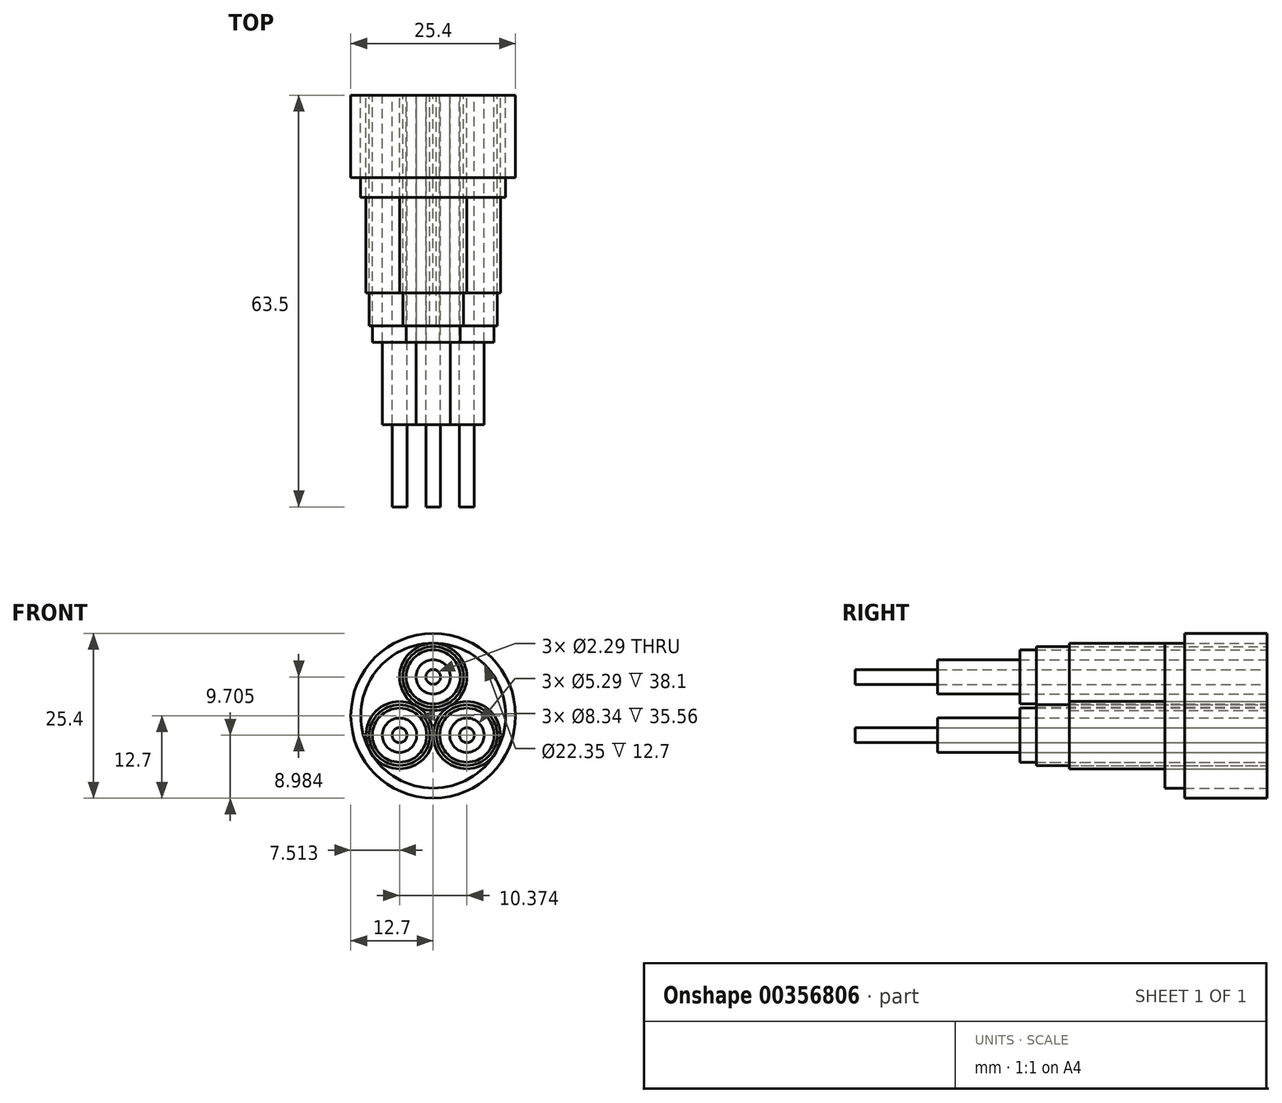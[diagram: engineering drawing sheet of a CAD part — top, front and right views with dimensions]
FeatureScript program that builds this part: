
annotation { "Feature Type Name" : "Feature", "Feature Type Description" : "" }
export const myFeature = defineFeature(function(context is Context, id is Id, definition is map)
    precondition{}
    {
        {
            var Q0;
            Q0=qCreatedBy(makeId("Front.planeOp"),FACE);
            var sketch = newSketch(context, id + "F0", { "sketchPlane" : qUnion([Q0])});
            skCircle(sketch, "E0", {"center": v(0, 0) * mm, "radius": 12.7 * mm});
            skCircle(sketch, "E1", {"center": v(0, 0) * mm, "radius": 11.18 * mm});
            skCircle(sketch, "E2", {"center": v(0, 5.99) * mm, "radius": 5.19 * mm});
            skCircle(sketch, "E3.1.0", {"center": v(-5.19, -3) * mm, "radius": 5.19 * mm, "construction": true});
            skCircle(sketch, "E3.2.0", {"center": v(5.19, -3) * mm, "radius": 5.19 * mm, "construction": true});
            skCircle(sketch, "E4", {"center": v(0, 5.99) * mm, "radius": 4.68 * mm});
            skCircle(sketch, "E5", {"center": v(0, 5.99) * mm, "radius": 4.17 * mm});
            skCircle(sketch, "E6", {"center": v(0, 5.99) * mm, "radius": 2.65 * mm});
            skCircle(sketch, "E7", {"center": v(0, 5.99) * mm, "radius": 1.14 * mm});
            skSolve(sketch);
        }
        {
            var Q0;
            Q0 = qSketchRegion(id + "F0", true);
            extrude(context, id + "F1", {"entities" : qUnion([Q0]), "depth" : 12.7 * mm});
        }
        {
            var Q0;
            Q0=makeQuery(id+"F0.imprint","IMPRINT",FACE,{"disambiguationData":[TD([[makeQuery(id+"F0.imprint","IMPRINT",EDGE,{"derivedFrom":sQuery(id+"F0.wireOp",EDGE,"E1")}),1.0]])]});
            var Q1;
            Q1=makeQuery(id+"F0.imprint","IMPRINT",FACE,{"disambiguationData":[TD([[makeQuery(id+"F0.imprint","IMPRINT",EDGE,{"derivedFrom":sQuery(id+"F0.wireOp",EDGE,"E7")}),1.0]])]});
            var Q2;
            Q2=makeQuery(id+"F0.imprint","IMPRINT",FACE,{"disambiguationData":[TD([[makeQuery(id+"F0.imprint","IMPRINT",EDGE,{"derivedFrom":sQuery(id+"F0.wireOp",EDGE,"E4")}),1.0]])]});
            var Q3;
            Q3=makeQuery(id+"F0.imprint","IMPRINT",FACE,{"disambiguationData":[TD([[makeQuery(id+"F0.imprint","IMPRINT",EDGE,{"derivedFrom":sQuery(id+"F0.wireOp",EDGE,"E5")}),1.0]])]});
            var Q4;
            Q4=makeQuery(id+"F0.imprint","IMPRINT",FACE,{"disambiguationData":[TD([[makeQuery(id+"F0.imprint","IMPRINT",EDGE,{"derivedFrom":sQuery(id+"F0.wireOp",EDGE,"E6")}),1.0]])]});
            var Q5;
            Q5=makeQuery(id+"F0.imprint","IMPRINT",FACE,{"disambiguationData":[TD([[makeQuery(id+"F0.imprint","IMPRINT",EDGE,{"derivedFrom":sQuery(id+"F0.wireOp",EDGE,"E2")}),1.0]])]});
            extrude(context, id + "F2", {"entities" : qUnion([Q0, Q1, Q2, Q3, Q4, Q5]), "depth" : 15.75 * mm});
        }
        {
            var Q0;
            Q0=makeQuery(id+"F0.imprint","IMPRINT",FACE,{"disambiguationData":[TD([[makeQuery(id+"F0.imprint","IMPRINT",EDGE,{"derivedFrom":sQuery(id+"F0.wireOp",EDGE,"E7")}),1.0]])]});
            var Q1;
            Q1=makeQuery(id+"F0.imprint","IMPRINT",FACE,{"disambiguationData":[TD([[makeQuery(id+"F0.imprint","IMPRINT",EDGE,{"derivedFrom":sQuery(id+"F0.wireOp",EDGE,"E2")}),1.0]])]});
            var Q2;
            Q2=makeQuery(id+"F0.imprint","IMPRINT",FACE,{"disambiguationData":[TD([[makeQuery(id+"F0.imprint","IMPRINT",EDGE,{"derivedFrom":sQuery(id+"F0.wireOp",EDGE,"E4")}),1.0]])]});
            var Q3;
            Q3=makeQuery(id+"F0.imprint","IMPRINT",FACE,{"disambiguationData":[TD([[makeQuery(id+"F0.imprint","IMPRINT",EDGE,{"derivedFrom":sQuery(id+"F0.wireOp",EDGE,"E5")}),1.0]])]});
            var Q4;
            Q4=makeQuery(id+"F0.imprint","IMPRINT",FACE,{"disambiguationData":[TD([[makeQuery(id+"F0.imprint","IMPRINT",EDGE,{"derivedFrom":sQuery(id+"F0.wireOp",EDGE,"E6")}),1.0]])]});
            extrude(context, id + "F3", {"entities" : qUnion([Q0, Q1, Q2, Q3, Q4]), "depth" : 30.48 * mm});
        }
        {
            var Q0;
            Q0=makeQuery(id+"F0.imprint","IMPRINT",FACE,{"disambiguationData":[TD([[makeQuery(id+"F0.imprint","IMPRINT",EDGE,{"derivedFrom":sQuery(id+"F0.wireOp",EDGE,"E4")}),1.0]])]});
            extrude(context, id + "F4", {"entities" : qUnion([Q0]), "depth" : 35.56 * mm});
        }
        {
            var Q0;
            Q0=makeQuery(id+"F0.imprint","IMPRINT",FACE,{"disambiguationData":[TD([[makeQuery(id+"F0.imprint","IMPRINT",EDGE,{"derivedFrom":sQuery(id+"F0.wireOp",EDGE,"E5")}),1.0]])]});
            extrude(context, id + "F5", {"entities" : qUnion([Q0]), "depth" : 38.1 * mm});
        }
        {
            var Q0;
            Q0=makeQuery(id+"F0.imprint","IMPRINT",FACE,{"disambiguationData":[TD([[makeQuery(id+"F0.imprint","IMPRINT",EDGE,{"derivedFrom":sQuery(id+"F0.wireOp",EDGE,"E6")}),1.0]])]});
            extrude(context, id + "F6", {"entities" : qUnion([Q0]), "depth" : 50.8 * mm});
        }
        {
            var Q0;
            Q0=makeQuery(id+"F0.imprint","IMPRINT",FACE,{"disambiguationData":[TD([[makeQuery(id+"F0.imprint","IMPRINT",EDGE,{"derivedFrom":sQuery(id+"F0.wireOp",EDGE,"E7")}),1.0]])]});
            extrude(context, id + "F7", {"entities" : qUnion([Q0]), "depth" : 63.5 * mm});
        }
        {
            var Q0;
            Q0=makeQuery(id+"F7.opExtrude","SWEPT_BODY",BODY,{"disambiguationData":[OSD([sQuery(id+"F0.wireOp",EDGE,"E7")])]});
            var Q1;
            Q1=makeQuery(id+"F4.opExtrude","SWEPT_BODY",BODY,{"disambiguationData":[OSD([sQuery(id+"F0.wireOp",EDGE,"E4"),sQuery(id+"F0.wireOp",EDGE,"E5")])]});
            var Q2;
            Q2=makeQuery(id+"F5.opExtrude","SWEPT_BODY",BODY,{"disambiguationData":[OSD([sQuery(id+"F0.wireOp",EDGE,"E5"),sQuery(id+"F0.wireOp",EDGE,"E6")])]});
            var Q3;
            Q3=makeQuery(id+"F6.opExtrude","SWEPT_BODY",BODY,{"disambiguationData":[OSD([sQuery(id+"F0.wireOp",EDGE,"E6"),sQuery(id+"F0.wireOp",EDGE,"E7")])]});
            var Q4;
            Q4=makeQuery(id+"F3.opExtrude","SWEPT_BODY",BODY,{"disambiguationData":[OSD([sQuery(id+"F0.wireOp",EDGE,"E2")])]});
            var Q5;
            Q5=makeQuery(id+"F2.opExtrude","CAP_EDGE",EDGE,{"disambiguationData":[OSD([sQuery(id+"F0.wireOp",EDGE,"E1")])],"isStart":false});
            circularPattern(context, id + "F8", {"entities" : qUnion([Q0, Q1, Q2, Q3, Q4]), "axis" : qUnion([Q5]), "angle" : 360 * degree, "instanceCount" : 3, "equalSpace" : true, "computeTransformsWithoutBuiltin" : true});
        }
    });
